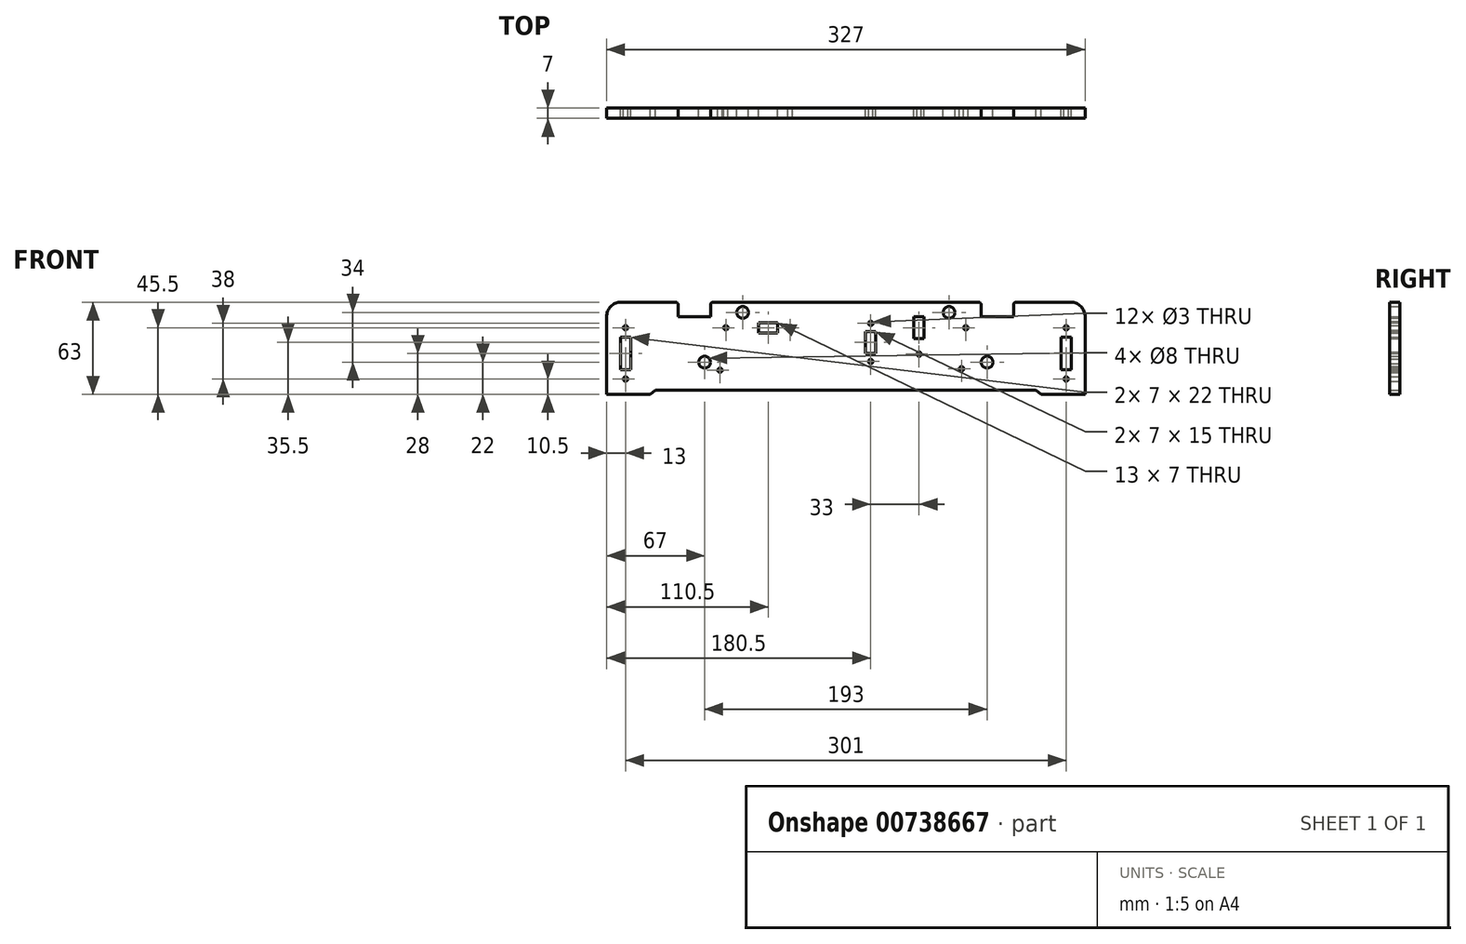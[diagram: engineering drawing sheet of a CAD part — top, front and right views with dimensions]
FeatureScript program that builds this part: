
annotation { "Feature Type Name" : "Feature", "Feature Type Description" : "" }
export const myFeature = defineFeature(function(context is Context, id is Id, definition is map)
    precondition{}
    {
        {
            var Q0;
            Q0=qCreatedBy(makeId("Front.planeOp"),FACE);
            var sketch = newSketch(context, id + "F0", { "sketchPlane" : qUnion([Q0])});
            skLineSegment(sketch, "E0", {"start": v(0, 0) * mm, "end": v(130, 0) * mm});
            skLineSegment(sketch, "E1", {"start": v(130, 0) * mm, "end": v(133.5, -3) * mm});
            skLineSegment(sketch, "E2", {"start": v(133.5, -3) * mm, "end": v(163.5, -3) * mm});
            skLineSegment(sketch, "E3", {"start": v(163.5, -3) * mm, "end": v(163.5, 50) * mm});
            skLineSegment(sketch, "E4", {"start": v(114.5, 58) * mm, "end": v(114.5, 50) * mm});
            skLineSegment(sketch, "E5", {"start": v(0, 60) * mm, "end": v(0, 0) * mm, "construction": true});
            skLineSegment(sketch, "E6", {"start": v(153.5, 60) * mm, "end": v(116.5, 60) * mm});
            skLineSegment(sketch, "E7", {"start": v(114.5, 50) * mm, "end": v(92.5, 50) * mm});
            skLineSegment(sketch, "E8", {"start": v(92.5, 50) * mm, "end": v(92.5, 58) * mm});
            skLineSegment(sketch, "E9", {"start": v(90.5, 60) * mm, "end": v(0, 60) * mm});
            skPoint(sketch, "E10.visualSharp", {"position": v(114.5, 60) * mm});
            skArc(sketch, "E10.filletArc", {"start": v(116.5, 60) * mm, "mid": v(115.09, 59.41) * mm, "end": v(114.5, 58) * mm});
            skPoint(sketch, "E11.visualSharp", {"position": v(92.5, 60) * mm});
            skArc(sketch, "E11.filletArc", {"start": v(92.5, 58) * mm, "mid": v(91.91, 59.41) * mm, "end": v(90.5, 60) * mm});
            skPoint(sketch, "E12.visualSharp", {"position": v(163.5, 60) * mm});
            skArc(sketch, "E12.filletArc", {"start": v(163.5, 50) * mm, "mid": v(160.57, 57.07) * mm, "end": v(153.5, 60) * mm});
            skLineSegment(sketch, "E13", {"start": v(150.5, -3) * mm, "end": v(150.5, 60) * mm, "construction": true});
            skLineSegment(sketch, "E14.bottom", {"start": v(154, 14) * mm, "end": v(147, 14) * mm});
            skLineSegment(sketch, "E14.top", {"start": v(154, 36) * mm, "end": v(147, 36) * mm});
            skLineSegment(sketch, "E14.left", {"start": v(154, 14) * mm, "end": v(154, 36) * mm});
            skLineSegment(sketch, "E14.right", {"start": v(147, 14) * mm, "end": v(147, 36) * mm});
            skPoint(sketch, "E14.middle", {"position": v(150.5, 25) * mm});
            skLineSegment(sketch, "E15", {"start": v(147, 25) * mm, "end": v(154, 25) * mm, "construction": true});
            skCircle(sketch, "E16", {"center": v(150.5, 42.5) * mm, "radius": 1.5 * mm});
            skCircle(sketch, "E17.MirrorC", {"center": v(150.5, 7.5) * mm, "radius": 1.5 * mm});
            skCircle(sketch, "E18", {"center": v(96.5, 19) * mm, "radius": 4 * mm});
            skCircle(sketch, "E19", {"center": v(70.5, 53) * mm, "radius": 4 * mm});
            skCircle(sketch, "E20", {"center": v(82, 42.5) * mm, "radius": 1.5 * mm});
            skArc(sketch, "E21.MirrorCS", {"start": v(-92.5, 58) * mm, "mid": v(-91.91, 59.41) * mm, "end": v(-90.5, 60) * mm});
            skArc(sketch, "E22.MirrorCS", {"start": v(-116.5, 60) * mm, "mid": v(-115.09, 59.41) * mm, "end": v(-114.5, 58) * mm});
            skLineSegment(sketch, "E23.MirrorCS", {"start": v(-92.5, 50) * mm, "end": v(-92.5, 58) * mm});
            skCircle(sketch, "E24.MirrorC", {"center": v(-82, 42.5) * mm, "radius": 1.5 * mm});
            skCircle(sketch, "E25.MirrorC", {"center": v(-150.5, 7.5) * mm, "radius": 1.5 * mm});
            skLineSegment(sketch, "E26.MirrorCS", {"start": v(-147, 14) * mm, "end": v(-147, 36) * mm});
            skLineSegment(sketch, "E27.MirrorCS", {"start": v(-130, 0) * mm, "end": v(-133.5, -3) * mm});
            skCircle(sketch, "E28.MirrorC", {"center": v(-150.5, 42.5) * mm, "radius": 1.5 * mm});
            skLineSegment(sketch, "E29.MirrorCS", {"start": v(-154, 36) * mm, "end": v(-147, 36) * mm});
            skLineSegment(sketch, "E30.MirrorCS", {"start": v(-154, 14) * mm, "end": v(-147, 14) * mm});
            skLineSegment(sketch, "E31.MirrorCS", {"start": v(-114.5, 58) * mm, "end": v(-114.5, 50) * mm});
            skLineSegment(sketch, "E32.MirrorCS", {"start": v(-154, 14) * mm, "end": v(-154, 36) * mm});
            skLineSegment(sketch, "E33.MirrorCS", {"start": v(-147, 25) * mm, "end": v(-154, 25) * mm, "construction": true});
            skCircle(sketch, "E34.MirrorC", {"center": v(-70.5, 53) * mm, "radius": 4 * mm});
            skArc(sketch, "E35.MirrorCS", {"start": v(-163.5, 50) * mm, "mid": v(-160.57, 57.07) * mm, "end": v(-153.5, 60) * mm});
            skLineSegment(sketch, "E36.MirrorCS", {"start": v(-150.5, -3) * mm, "end": v(-150.5, 60) * mm, "construction": true});
            skLineSegment(sketch, "E37.MirrorCS", {"start": v(-90.5, 60) * mm, "end": v(0, 60) * mm});
            skLineSegment(sketch, "E38.MirrorCS", {"start": v(-153.5, 60) * mm, "end": v(-116.5, 60) * mm});
            skLineSegment(sketch, "E39.MirrorCS", {"start": v(-163.5, -3) * mm, "end": v(-163.5, 50) * mm});
            skLineSegment(sketch, "E40.MirrorCS", {"start": v(-114.5, 50) * mm, "end": v(-92.5, 50) * mm});
            skLineSegment(sketch, "E41.MirrorCS", {"start": v(-133.5, -3) * mm, "end": v(-163.5, -3) * mm});
            skPoint(sketch, "E42.MirrorP", {"position": v(-163.5, 60) * mm});
            skLineSegment(sketch, "E43.MirrorCS", {"start": v(0, 0) * mm, "end": v(-130, 0) * mm});
            skCircle(sketch, "E44.MirrorC", {"center": v(-96.5, 19) * mm, "radius": 4 * mm});
            skPoint(sketch, "E45.MirrorP", {"position": v(-92.5, 60) * mm});
            skPoint(sketch, "E46.MirrorP", {"position": v(-150.5, 25) * mm});
            skPoint(sketch, "E47.MirrorP", {"position": v(-114.5, 60) * mm});
            skLineSegment(sketch, "E48.bottom", {"start": v(-46.5, 46) * mm, "end": v(-59.5, 46) * mm});
            skLineSegment(sketch, "E48.top", {"start": v(-46.5, 39) * mm, "end": v(-59.5, 39) * mm});
            skLineSegment(sketch, "E48.left", {"start": v(-46.5, 46) * mm, "end": v(-46.5, 39) * mm});
            skLineSegment(sketch, "E48.right", {"start": v(-59.5, 46) * mm, "end": v(-59.5, 39) * mm});
            skPoint(sketch, "E48.middle", {"position": v(-53, 42.5) * mm});
            skCircle(sketch, "E49", {"center": v(-38, 42.5) * mm, "radius": 1.5 * mm});
            skCircle(sketch, "E50", {"center": v(-86, 13.5) * mm, "radius": 1.5 * mm});
            skLineSegment(sketch, "E51.bottom", {"start": v(20.5, 25) * mm, "end": v(13.5, 25) * mm});
            skLineSegment(sketch, "E51.top", {"start": v(20.5, 40) * mm, "end": v(13.5, 40) * mm});
            skLineSegment(sketch, "E51.left", {"start": v(20.5, 25) * mm, "end": v(20.5, 40) * mm});
            skLineSegment(sketch, "E51.right", {"start": v(13.5, 25) * mm, "end": v(13.5, 40) * mm});
            skPoint(sketch, "E51.middle", {"position": v(17, 32.5) * mm});
            skLineSegment(sketch, "E52.bottom", {"start": v(46.5, 50) * mm, "end": v(53.5, 50) * mm});
            skLineSegment(sketch, "E52.top", {"start": v(46.5, 35) * mm, "end": v(53.5, 35) * mm});
            skLineSegment(sketch, "E52.left", {"start": v(46.5, 50) * mm, "end": v(46.5, 35) * mm});
            skLineSegment(sketch, "E52.right", {"start": v(53.5, 50) * mm, "end": v(53.5, 35) * mm});
            skPoint(sketch, "E52.middle", {"position": v(50, 42.5) * mm});
            skCircle(sketch, "E53", {"center": v(50, 24.5) * mm, "radius": 1.5 * mm});
            skCircle(sketch, "E54", {"center": v(17, 19.5) * mm, "radius": 1.5 * mm});
            skLineSegment(sketch, "E55", {"start": v(13.5, 32.5) * mm, "end": v(20.5, 32.5) * mm, "construction": true});
            skCircle(sketch, "E56.MirrorC", {"center": v(17, 45.5) * mm, "radius": 1.5 * mm});
            skCircle(sketch, "E57", {"center": v(79, 14.5) * mm, "radius": 1.5 * mm});
            skSolve(sketch);
        }
        {
            var Q0;
            Q0 = qSketchRegion(id + "F0", true);
            extrude(context, id + "F1", {"entities" : qUnion([Q0]), "depth" : 7 * mm, "offsetDistance" : 25 * mm});
        }
    });
